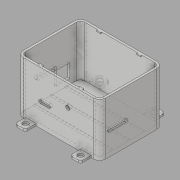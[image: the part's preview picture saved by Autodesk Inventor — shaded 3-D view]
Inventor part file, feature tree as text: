
AUTODESK INVENTOR PART (.ipt)
format: ipt  version: 2017 (Build 210142000, 142)  size: 254,976 bytes
history: native  units: mm
features: extrude x10, sketch x10, thicken_offset x1, other x1
ambient origin geometry x8: Origin, YZ Plane, XZ Plane, XY Plane, X Axis, Y Axis, Z Axis, Center Point
bodies: Solid1 (feature_tree)
feature tree (22):
  thicken_offset  "Thicken1"
  extrude  "Bottom"  Depth=50.0mm TaperAngle=0.0deg
  extrude  "Mounting Tabs"  Depth=2.0mm
  extrude  "Mounting Tab Holes"  Depth=2.0mm TaperAngle=0.0deg
  extrude  "Bottom Ridges"  Depth=1.0mm TaperAngle=0.0deg
  extrude  "Bottom Latch"  Depth=2.0mm
  extrude  "Top Latch"  Depth=2.0mm
  extrude  "R Holes"  Depth=5.0mm
  extrude  "L Holes"  Depth=2.0mm TaperAngle=0.0deg
  extrude  "Top Holes"  Depth=16.0mm
  sketch  "Sketch1"  dims[d0=4.0mm d1=50.0mm d2=0.0mm]
  other  "Srf1"
  sketch  "Sketch2"  dims[d3=2.0mm d4=2.0mm]
  sketch  "Sketch4"  dims[d5=4.0mm d6=2.0mm d7=0.0mm]
  sketch  "Sketch6"  dims[d8=76.0mm d9=0.0mm d10=1.0mm d11=0.0mm]
  sketch  "Sketch8"  dims[d16=1.0mm d17=0.0mm d18=2.0mm]
  sketch  "Sketch9"  dims[d19=2.0mm d20=0.0mm d21=5.0mm]
  sketch  "Sketch10"  dims[d22=5.0mm d23=5.0mm]
  sketch  "Sketch11"  dims[d24=5.0mm d25=2.0mm d26=0.0mm]
  sketch  "Sketch12"  dims[d27=2.0mm d28=0.0mm d29=16.0mm]
  sketch  "Sketch13"  dims[d30=3.0mm d31=16.0mm d32=3.0mm d33=2.0mm d34=0.0mm d35=8.0mm d36=3.0mm d37=2.0mm d38=0.0mm d42=3.0mm]
  extrude  "ExtrusionSrf1"  Depth=16.0mm
